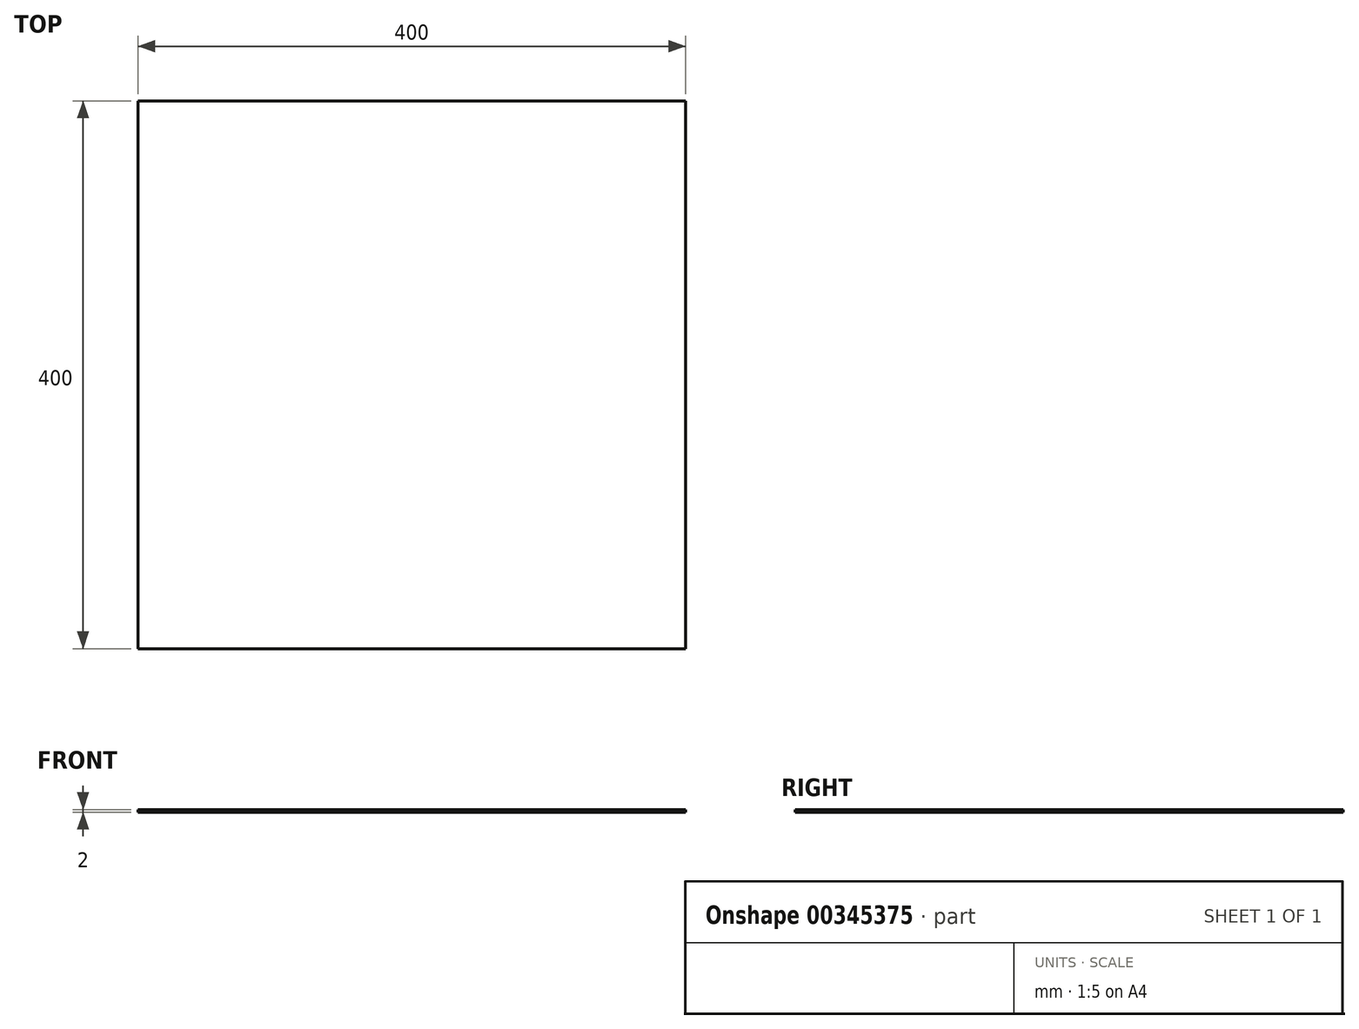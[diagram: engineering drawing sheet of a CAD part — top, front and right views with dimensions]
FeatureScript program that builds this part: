
annotation { "Feature Type Name" : "Feature", "Feature Type Description" : "" }
export const myFeature = defineFeature(function(context is Context, id is Id, definition is map)
    precondition{}
    {
        {
            var Q0;
            Q0=qCreatedBy(makeId("Top.planeOp"),FACE);
            var sketch = newSketch(context, id + "F0", { "sketchPlane" : qUnion([Q0])});
            skLineSegment(sketch, "E0.bottom", {"start": v(-195.86, -133.35) * mm, "end": v(204.14, -133.35) * mm});
            skLineSegment(sketch, "E0.top", {"start": v(-195.86, 266.65) * mm, "end": v(204.14, 266.65) * mm});
            skLineSegment(sketch, "E0.left", {"start": v(-195.86, -133.35) * mm, "end": v(-195.86, 266.65) * mm});
            skLineSegment(sketch, "E0.right", {"start": v(204.14, -133.35) * mm, "end": v(204.14, 266.65) * mm});
            skSolve(sketch);
        }
        {
            var Q0;
            Q0=makeQuery(id+"F0.imprint","IMPRINT",FACE,{"disambiguationData":[TD([[makeQuery(id+"F0.imprint","IMPRINT",EDGE,{"derivedFrom":sQuery(id+"F0.wireOp",EDGE,"E0.bottom")}),1.0]])]});
            extrude(context, id + "F1", {"entities" : qUnion([Q0]), "depth" : 2 * mm});
        }
    });
